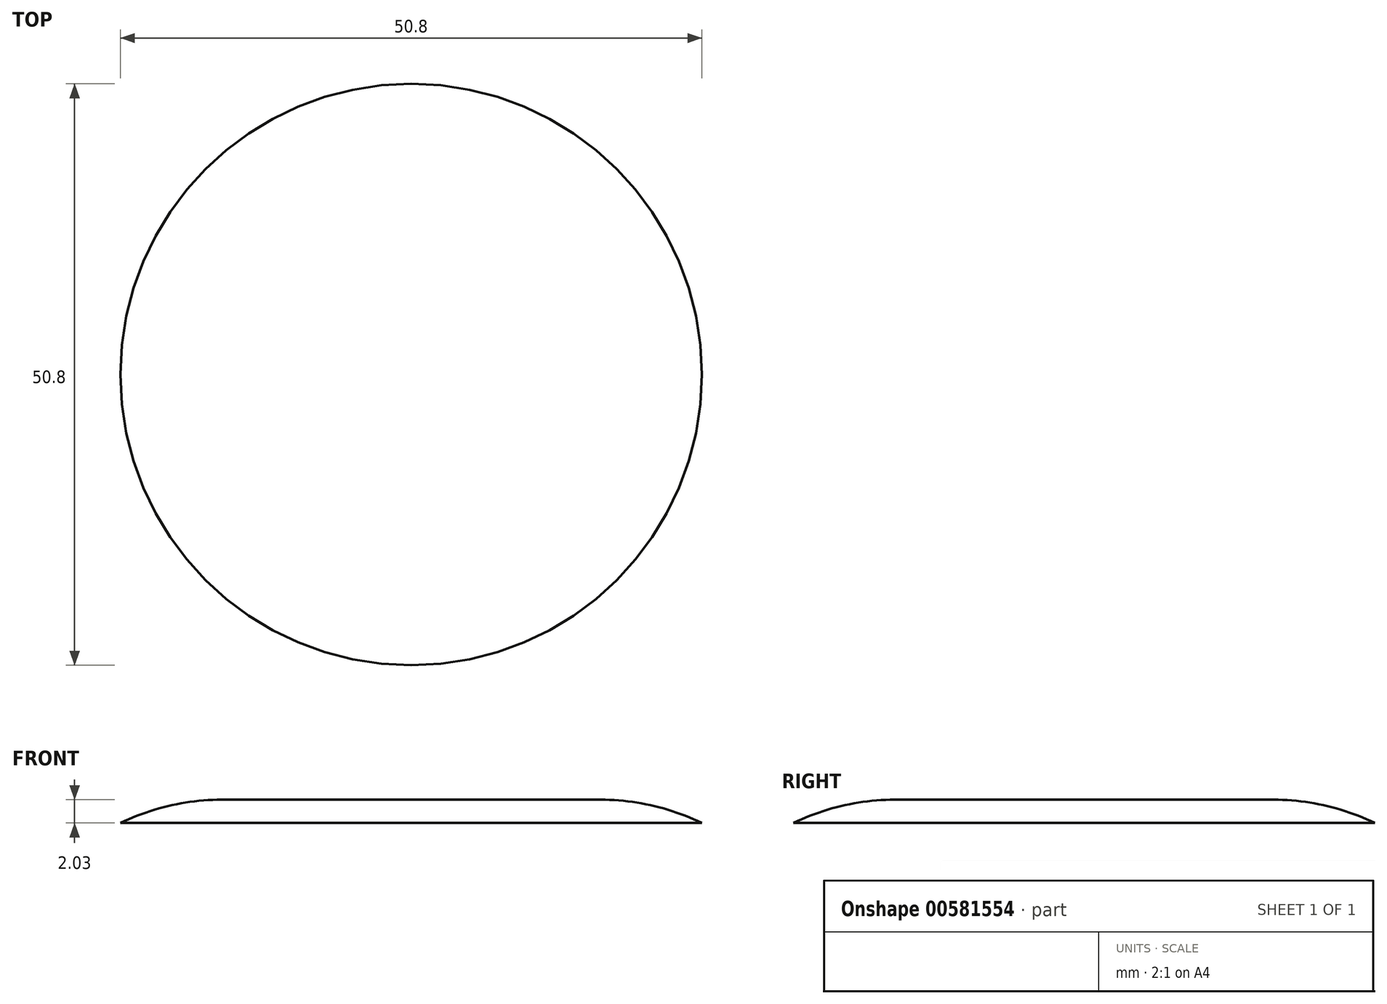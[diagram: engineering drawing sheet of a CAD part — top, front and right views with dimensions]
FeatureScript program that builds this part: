
annotation { "Feature Type Name" : "Feature", "Feature Type Description" : "" }
export const myFeature = defineFeature(function(context is Context, id is Id, definition is map)
    precondition{}
    {
        {
            var Q0;
            Q0=qCreatedBy(makeId("Top.planeOp"),FACE);
            var sketch = newSketch(context, id + "F0", { "sketchPlane" : qUnion([Q0])});
            skCircle(sketch, "E0", {"center": v(0, 0) * mm, "radius": 25.4 * mm});
            skSolve(sketch);
        }
        {
            var Q0;
            Q0=makeQuery(id+"F0.imprint","IMPRINT",FACE,{"disambiguationData":[TD([[makeQuery(id+"F0.imprint","IMPRINT",EDGE,{"derivedFrom":sQuery(id+"F0.wireOp",EDGE,"E0")}),1.0]])]});
            extrude(context, id + "F1", {"entities" : qUnion([Q0]), "depth" : 2.03 * mm, "offsetDistance" : 25.4 * mm});
        }
        {
            var Q0;
            Q0=makeQuery(id+"F1.opExtrude","CAP_EDGE",EDGE,{"disambiguationData":[OSD([sQuery(id+"F0.wireOp",EDGE,"E0")])],"isStart":false});
            fillet(context, id + "F2", {"entities" : qUnion([Q0]), "radius" : 20.32 * mm, "tangentPropagation" : true, "allowEdgeOverflow" : false});
        }
    });
